# Revit family: IS_Ceraline_BC822_BIM_NL
name_source: partatom
category: Plumbing Fixtures
units: mm (PartAtom-declared; Revit-internal decimal feet)

## family parameters
Always vertical = No
Cut with Voids When Loaded = No
OmniClass Number = 23.45.55.17
OmniClass Title = Mixing Faucets
Part Type = Normal
Room Calculation Point = No
Round Connector Dimension = Use Diameter
Shared = No
Work Plane-Based = No

## types (2) — shared parameters
Accesoires = https://www.idealstandard.nl
Accessories = https://www.idealstandard.nl
Afmetingen = 50 x 135 x 148 mm
AfstandsEenheid = Millimeter
AreaMeasurement = Internal
AreaUnits = Millimeter
Artikelreferentie = CERALINE WASCHTISCHMISCHER RIM-MONTIERTER CLICK ABFALL 5L PRO MINUTE
Auteur = Ideal Standard
BIMObjectName = IS_IdealStandard_Washbasintaps_Ceraline_BC822
BIMobject category = Sanitary
BIMobject category code = Sanitary Taps & Mixer
BIMobject main category = Sanitary
BIMobject main category code = Sanitary
Bedieningkraan = Handbuch
Bedieningkraanwerk = einzelne Ebene
Beschrijvinggarantie = Herstellergarantie
BimObjectNaam = IS_IdealStandard_Washbasintaps_Ceraline_BC822
Brand = Ideal Standard
Brand url = http://www.idealstandard.nl
Breedte = 50.120245
ConnectionType = plumbing
CurrencyUnit = €
CurrentRevision = 1
Date of publishing = 01/07/2021
Diepte = 135 mm
DikteMateriaal = Messing
Doorstromingscoëfficiënt = 5L/min
Douchebak = No
DurationUnit = Years
DuurEenheid = Jaren
Edition number = 1
FaucetFunction = Washbasin Mixer
FaucetOperation = Manual Lever mixer
FaucetTopDescription = Lever mixer
FaucetType = Washbasin Mixer
Functiekraanwerk = Einhebelgriff
Garantieunits = Jaren
GemaaktOp = 22/07/2021
Help = https://www.idealstandard.nl
Hoogte = 147.513683895115
Hulp = https://www.idealstandard.nl
IFC Classification = Sanitary Terminal
IfcExportAs = IfcValveType
IfcExportType = FAUCET
Installatieinstructies = https://www.idealstandard.nl
Installation instructions = https://www.idealstandard.nl
InstallationInstructions = https://www.idealstandard.nl
IsBuiltIn = No
IsHighPressure = No
Lengte = 135 mm
LinearUnits = Millimeters
MaintenanceInformation = https://www.idealstandard.nl
Manufacturer = Ideal Standard
Manufacturer name = Ideal Standard
ManufacturerURL = https://www.idealstandard.nl
Masterformat 2014 Code = 41 14 33
Masterformat 2014 Description = Mixer
Materiaal = Messing
Material = Brass
Material main = Brass
Merk = Ideal Standard
ModelReference = CERALINE BASIN MIXER RIM-MOUNTED CLICK WASTE 5L PER MINUTE
Montageinstuctie = https://www.idealstandard.nl
NBS Reference Code = 45-35-70/371
NBS Reference Description = Water supply fittings for wash basins and troughs
Name = Washbasintaps_Ceraline_BC822_IdealStandard
NominalHeight = 148 mm
NominalLength = 135 mm
NominalWidth = 50 mm  [stored 0.164042 ft]
Normen = Washbasintaps_Ceraline_BC822_IdealStandard
OmniClass Code = 23-31 11 00
OmniClass Description = Faucets
OppervlakteEenheid = Millimeter
Product Guid = 1caf4936-0128-4703-9ac2-c1ffa1d77b6e
Product SKU = BC822
Product certification = https://www.idealstandard.nl
Product data url = https://bimobject.com
Product family = Ceraline
Product group = Taps & Mixers
Product name = CERALINE BASIN MIXER RIM-MOUNTED CLICK WASTE 5L PER MINUTE
Product url = https://www.idealstandard.nl
ProductInformation = https://www.idealstandard.nl
ProductSoort = Armaturen Mixer
Productinformatie = https://www.idealstandard.nl
QR code = http://bimobject.com
Referentie = CERALINE BASIN MIXER RIM-MOUNTED CLICK WASTE 5L PER MINUTE
Revisie = 1
Shape = Cylindrical
Size = 50 x 135 x 148 mm
Space = Internal
SpareParts = https://www.idealstandard.nl
Technical description = https://www.idealstandard.nl
Telefoonnummer = 077 355 08 08
TestPressure = 10 Bar
Testdruk = 10 Bar
Typeconnectie = Installation
UNSPSC Code = 301815
URL = https://www.idealstandard.nl
Uniclass 1.4 Code = L725111
Uniclass 1.4 Description = Mixers taps
Uniclass 2.0 Code = PR-35-79-95
Uniclass 2.0 Description = Wash Basin and trough Water Supply Fittings
Uniclass 2015 Code = Pr_40_20_87_98
Uniclass 2015 Name = Washbasin taps
Uniclass2015Code = Pr_40_20_87_98
Uniclass2015Title = Washbasin taps
Uniclass2015Version = v1.20
Urlproducent = https://www.idealstandard.nl
ValutaEenheid = Euro
Versie = 1
Version = 1
VolumeUnits = Liters
Volumeunits = Liter
Vorm = zylindrisch
WRASURL = https://www.wrasapprovals.co.uk
WarrantyDescription = manufacturer warranty
WarrantyDurationParts = 5
WarrantyDurationUnit = Years
Wisselstukken = https://www.idealstandard.nl
Youtube clip = https://www.youtube.com
zero-valued in all types: BrutoGewicht, Cost, DrainSize, InletConnectionSize, MaterialThickness, OutletConnectionSize, Overloop, Vervangingskosten

## per-type parameters (varying)
| type | Afwerking | Artikelnummer | Artikelomschrijving | BarCode | Barcode | Color | Description | Eigenschappen | Features | Finish | GTIN code | Kleur | MainColor | Model | ModelNumber | NettWeight | Nettogewicht |
| BC822AA - CERALINE BASIN MIXER RIM-MOUNTED CLICK WASTE 5L PER MINUTE - CHROME | chrom | BC822AA | CERALINE WASCHTISCHMISCHER RIM-MONTIERTER CLICK ABFALL 5L PRO MINUTE - CHROM | 3800861083993 | 3800861083993 | chrom | CERALINE BASIN MIXER RIM-MOUNTED CLICK WASTE 5L PER MINUTE - CHROME | WASCHTISCHMISCHER RIM-MONTIERTER CLICK ABFALL 5L PRO MINUTE - CHROM | BASIN MIXER RIM-MOUNTED CLICK WASTE 5L PER MINUTE - CHROME | chrom | https://3800861083993 | chrom | CHROME | BC822AA | BC822AA | 1.21 | 1.21 |
| BC822XG - CERALINE BASIN MIXER RIM-MOUNTED CLICK WASTE 5L PER MINUTE - SILK BLACK | seide schwarz | BC822XG | CERALINE WASCHTISCHMISCHER RIM-MONTIERTER CLICK ABFALL 5L PRO MINUTE - SEIDE SCHWARZ | 3800861101468 | 3800861101468 | seide schwarz | CERALINE BASIN MIXER RIM-MOUNTED CLICK WASTE 5L PER MINUTE - SILK BLACK | WASCHTISCHMISCHER RIM-MONTIERTER CLICK ABFALL 5L PRO MINUTE - SEIDE SCHWARZ | BASIN MIXER RIM-MOUNTED CLICK WASTE 5L PER MINUTE - SILK BLACK | seide schwarz | https://3800861101468 | seide schwarz | SILK BLACK | BC822XG | BC822XG | 1.31 | 1.31 |

note: [stored X ft] marks values corroborated as IEEE doubles in the binary element streams (Revit-internal decimal feet)

## geometry (parser evidence)
native form markers: Sweep x3
no freeform markers — native parametric forms only
